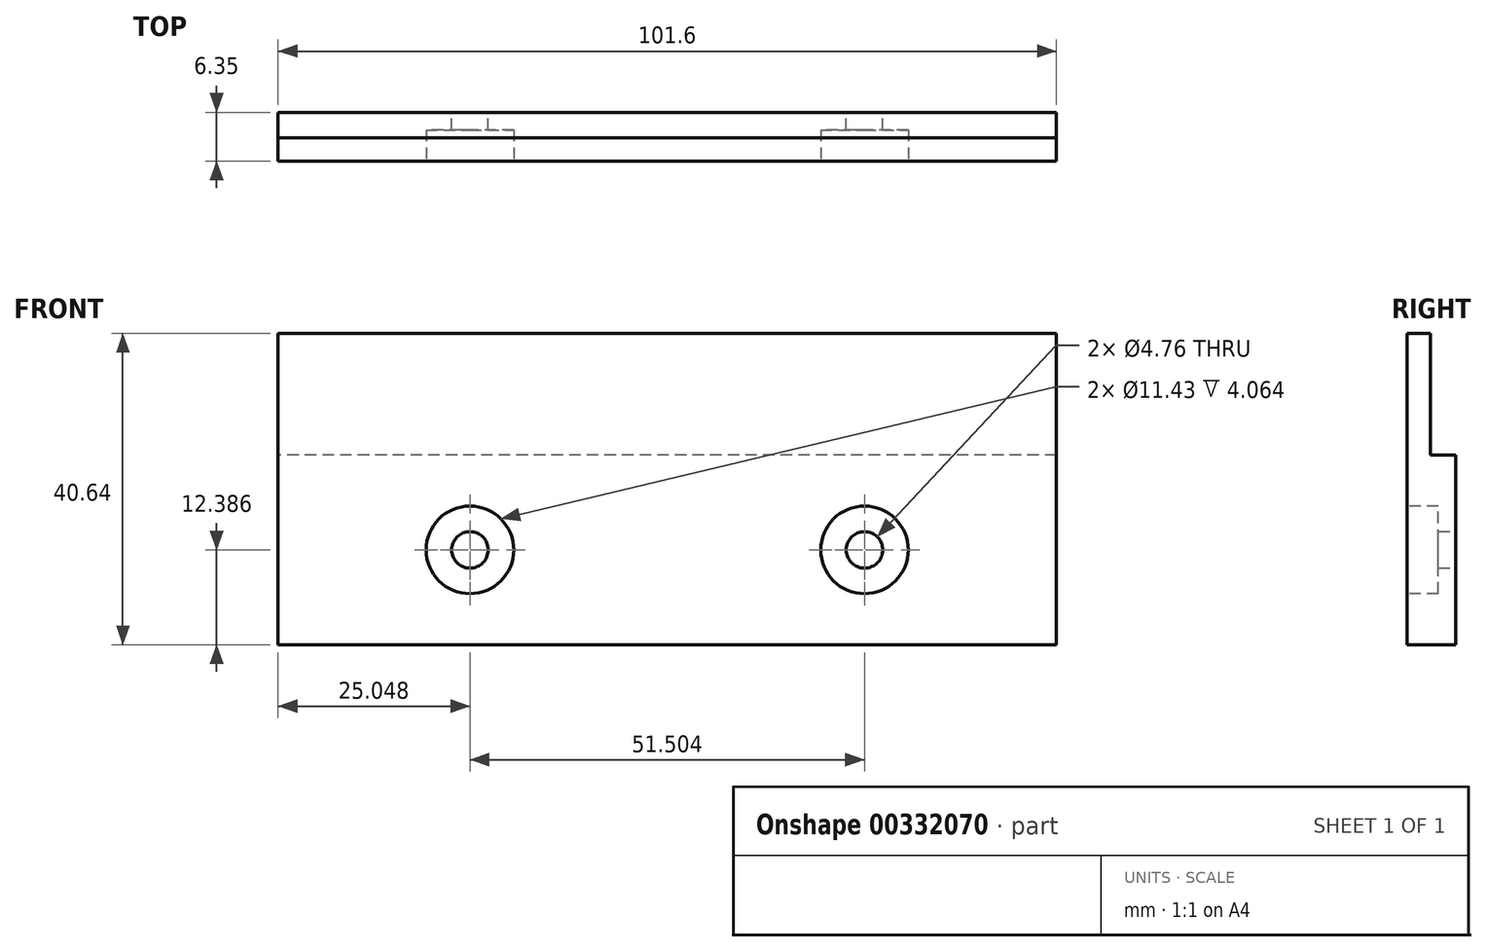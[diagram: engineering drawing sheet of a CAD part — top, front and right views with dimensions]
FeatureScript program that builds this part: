
annotation { "Feature Type Name" : "Feature", "Feature Type Description" : "" }
export const myFeature = defineFeature(function(context is Context, id is Id, definition is map)
    precondition{}
    {
        {
            var Q0;
            Q0=qCreatedBy(makeId("Right.planeOp"),FACE);
            var sketch = newSketch(context, id + "F0", { "sketchPlane" : qUnion([Q0])});
            skLineSegment(sketch, "E0", {"start": v(0, -15.32) * mm, "end": v(-3, -15.32) * mm});
            skLineSegment(sketch, "E1", {"start": v(-3, -15.32) * mm, "end": v(-3, -55.96) * mm});
            skLineSegment(sketch, "E2", {"start": v(-3, -55.96) * mm, "end": v(3.35, -55.96) * mm});
            skLineSegment(sketch, "E3", {"start": v(3.35, -55.96) * mm, "end": v(3.35, -31.2) * mm});
            skLineSegment(sketch, "E4", {"start": v(3.35, -31.2) * mm, "end": v(0, -31.2) * mm});
            skLineSegment(sketch, "E5", {"start": v(0, -31.2) * mm, "end": v(0, -15.32) * mm});
            skSolve(sketch);
        }
        {
            var Q0;
            Q0 = qSketchRegion(id + "F0", true);
            extrude(context, id + "F1", {"entities" : qUnion([Q0]), "depth" : 101.6 * mm});
        }
        {
            var Q0;
            Q0=makeQuery(id+"F1.opExtrude","SWEPT_FACE",FACE,{"disambiguationData":[OSD([sQuery(id+"F0.wireOp",EDGE,"E3")])]});
            var sketch = newSketch(context, id + "F2", { "sketchPlane" : qUnion([Q0])});
            skLineSegment(sketch, "E6", {"start": v(-50.8, -31.2) * mm, "end": v(-50.8, -55.96) * mm, "construction": true});
            skCircle(sketch, "E7", {"center": v(-76.55, -43.57) * mm, "radius": 2.38 * mm});
            skPoint(sketch, "E7.centerSnap0", {"position": v(-101.6, -43.57) * mm});
            skCircle(sketch, "E8.MirrorC", {"center": v(-25.05, -43.57) * mm, "radius": 2.38 * mm});
            skSolve(sketch);
        }
        {
            var Q0;
            Q0 = qSketchRegion(id + "F2", true);
            extrude(context, id + "F3", {"entities" : qUnion([Q0]), "operationType" : NewBodyOperationType.REMOVE, "endBound" : BoundingType.UP_TO_NEXT, "oppositeDirection" : true, "depth" : 25.4 * mm});
        }
        {
            var Q0;
            Q0=makeQuery(id+"F1.opExtrude","SWEPT_FACE",FACE,{"disambiguationData":[OSD([sQuery(id+"F0.wireOp",EDGE,"E1")])]});
            var sketch = newSketch(context, id + "F4", { "sketchPlane" : qUnion([Q0])});
            skCircle(sketch, "E9", {"center": v(25.05, -43.57) * mm, "radius": 5.72 * mm});
            skCircle(sketch, "E10", {"center": v(76.55, -43.57) * mm, "radius": 5.72 * mm});
            skSolve(sketch);
        }
        {
            var Q0;
            Q0 = qSketchRegion(id + "F4", true);
            extrude(context, id + "F5", {"entities" : qUnion([Q0]), "operationType" : NewBodyOperationType.REMOVE, "oppositeDirection" : true, "depth" : 4.06 * mm});
        }
    });
